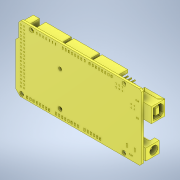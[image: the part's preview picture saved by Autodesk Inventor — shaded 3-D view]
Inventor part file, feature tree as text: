
AUTODESK INVENTOR PART (.ipt)
format: ipt  version: 2020 (Build 240168000, 168)  size: 1,245,696 bytes
history: native  units: in
note: dims shown in document units (in); Inventor stores cm internally (conversion verified against a paired STEP export)
features: sketch x1, fillet x1
ambient origin geometry x8: Origin, YZ Plane, XZ Plane, XY Plane, X Axis, Y Axis, Z Axis, Center Point
bodies: Solid1 (feature_tree)
feature tree (2):
  sketch  "Sketch1"
  fillet  "Fillet5"  [1 undecoded]
note: 1 required parameter value undecoded (feature->parameter linkage not recoverable at this tier; creation-order binding heuristic only, values carry confidence <= 0.55)
